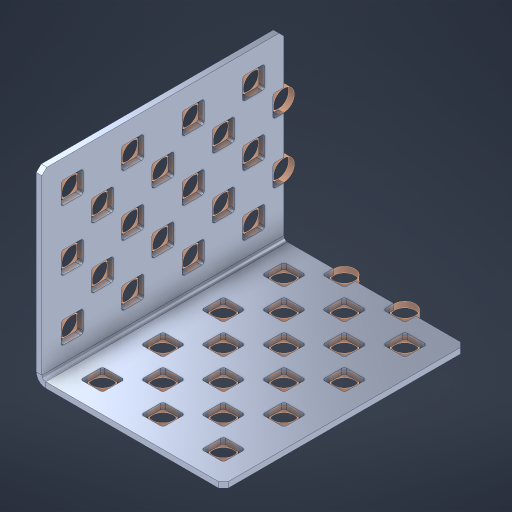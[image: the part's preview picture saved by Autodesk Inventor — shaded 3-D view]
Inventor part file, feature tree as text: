
AUTODESK INVENTOR PART (.ipt)
format: ipt  version: 2023 (Build 270158000, 158)  size: 741,376 bytes
history: native  units: in
note: dims shown in document units (in); Inventor stores cm internally (conversion verified against a paired STEP export)
features: other x46, extrude x38, sheet_metal_op x8, sketch x7, pattern_linear x3, mirror x1, chamfer x1
ambient origin geometry x8: Origin, YZ Plane, XZ Plane, XY Plane, X Axis, Y Axis, Z Axis, Center Point
bodies: Solid1 (feature_tree), Body (feature_tree)
feature tree (104):
  sheet_metal_op  "Flanges"
  sheet_metal_op  "Body Pattern"
  pattern_linear  "Center Double"  Spacing1=1.5in  [1 undecoded]
  pattern_linear  "Center Pattern"  Spacing1=0.1875in  [1 undecoded]
  other  "Arc Length"
  pattern_linear  "Notch Pattern"  Spacing1=0.0469in  [1 undecoded]
  other  "Diagonal Plane"
  mirror  "Everything Mirrored"
  chamfer  "End Chamfer"
  sketch  "Sketch1"  dims[d0=1.5in]
  other  "Plate1"
  sketch  "Sketch2"  dims[d1=2.0in]
  other  "Plate2"
  sheet_metal_op  "Bend1"
  sheet_metal_op  "Corner1"
  sketch  "Sketch8"  dims[d2=0.0469in]
  sketch  "Sketch9"  dims[d3=0.0469in]
  other  "Srf91"
  sheet_metal_op  "Body Pattern Sketch"
  other  "Srf92"
  sketch  "Sketch13"  dims[d4=0.0234in]
  sketch  "Sketch15"  dims[d5=0.0938in]
  sketch  "Sketch16"  dims[d6=0.0469in d7=1.5in d8=90.0deg d9=0.0312in d10=0.1875in d11=0.0469in d12=0.0469in d49=0.182in d50=0.02in d52=0.25in d53=0.0469in d54=0.0in d55=0.172in d56=1.0in d57=0.0in d85=0.1473in d86=0.1659in d89=0.0469in d90=0.0in d91=0.04in d92=0.0491in d95=2.5in d96=0.04in d97=0.25in d98=45.0deg d106=0.182in d107=0.02in d110=0.0469in d111=0.0in d112=0.172in d113=0.5in d114=0.0in d117=0.5in d126=0.0491in d127=0.1227in d128=0.08in d129=0.04in d130=2.5in d131=0.25in d132=1.5748in d134=0.5in d135=1.1811in d137=0.5in d140=0.5in d141=1.0in d142=0.3937in d144=0.5in d145=0.071in d146=0.7874in d148=0.5in]
  other  "Srf786"
  other  "Srf856"
  other  "Srf889"
  other  "Srf890"
  other  "Srf891"
  other  "Srf1275"
  other  "Srf1276"
  other  "Srf1278"
  other  "Srf1277"
  other  "Srf1285"
  other  "Srf1286"
  other  "Srf1287"
  other  "Srf2009"
  other  "Srf2010"
  other  "Srf2011"
  other  "Srf2012"
  other  "Srf2043"
  other  "Srf2044"
  other  "Srf2045"
  other  "Srf2076"
  other  "Srf2077"
  other  "Srf2078"
  other  "Srf2079"
  other  "Srf2080"
  other  "Srf2081"
  other  "Srf2082"
  other  "Srf2083"
  other  "Srf2084"
  other  "Srf2085"
  other  "Srf2179"
  other  "Srf2180"
  other  "Srf2181"
  other  "Srf2182"
  other  "Srf2183"
  other  "Srf2184"
  other  "Srf2185"
  other  "Srf2186"
  other  "Srf2187"
  sheet_metal_op  "Body Stamp"
  sheet_metal_op  "Body Circle"
  other  "Center Stamp"
  other  "Center Circle"
  sheet_metal_op  "Notch"
  extrude  "ExtrusionSrf92"  Depth=0.0469in
  extrude  "ExtrusionSrf856"  Depth=0.182in
  extrude  "ExtrusionSrf889"  Depth=0.02in
  extrude  "ExtrusionSrf890"  Depth=0.25in
  extrude  "ExtrusionSrf891"  Depth=0.0469in
  extrude  "ExtrusionSrf1275"  TaperAngle=0.0deg  [1 undecoded]
  extrude  "ExtrusionSrf1276"  Depth=0.5in
  extrude  "ExtrusionSrf1277"  Depth=1.0in TaperAngle=0.0deg
  extrude  "ExtrusionSrf1345"  Depth=0.5in
  extrude  "ExtrusionSrf1346"  Depth=0.5in
  extrude  "ExtrusionSrf1347"  Depth=0.0469in
  extrude  "ExtrusionSrf1348"  Depth=0.5in TaperAngle=0.0deg
  extrude  "ExtrusionSrf2009"  Depth=0.5in
  extrude  "ExtrusionSrf2010"  Depth=0.25in TaperAngle=45.0deg
  extrude  "ExtrusionSrf2011"  Depth=0.182in
  extrude  "ExtrusionSrf2012"  Depth=0.02in
  extrude  "ExtrusionSrf2043"  Depth=0.0469in
  extrude  "ExtrusionSrf2044"  TaperAngle=0.0deg  [1 undecoded]
  extrude  "ExtrusionSrf2045"  Depth=0.5in
  extrude  "ExtrusionSrf2076"  Depth=0.5in TaperAngle=0.0deg
  extrude  "ExtrusionSrf2077"  Depth=0.5in
  extrude  "ExtrusionSrf2078"  Depth=0.5in
  extrude  "ExtrusionSrf2079"  Depth=0.5in
  extrude  "ExtrusionSrf2080"  Depth=0.5in
  extrude  "ExtrusionSrf2081"  Depth=0.5in
  extrude  "ExtrusionSrf2082"  Depth=0.5in
  extrude  "ExtrusionSrf2083"  Depth=0.25in
  extrude  "ExtrusionSrf2084"  Depth=0.5in
  extrude  "ExtrusionSrf2085"  Depth=0.5in
  extrude  "ExtrusionSrf2179"  Depth=0.5in
  extrude  "ExtrusionSrf2180"  Depth=1.0in
  extrude  "ExtrusionSrf2181"  Depth=0.3937in
  extrude  "ExtrusionSrf2182"  Depth=0.5in
  extrude  "ExtrusionSrf2183"  Depth=0.5in
  extrude  "ExtrusionSrf2184"  [1 undecoded]
  extrude  "ExtrusionSrf2185"  [1 undecoded]
  extrude  "ExtrusionSrf2186"  [1 undecoded]
  extrude  "ExtrusionSrf2187"  [1 undecoded]
note: 9 required parameter values undecoded (feature->parameter linkage not recoverable at this tier; creation-order binding heuristic only, values carry confidence <= 0.55)
